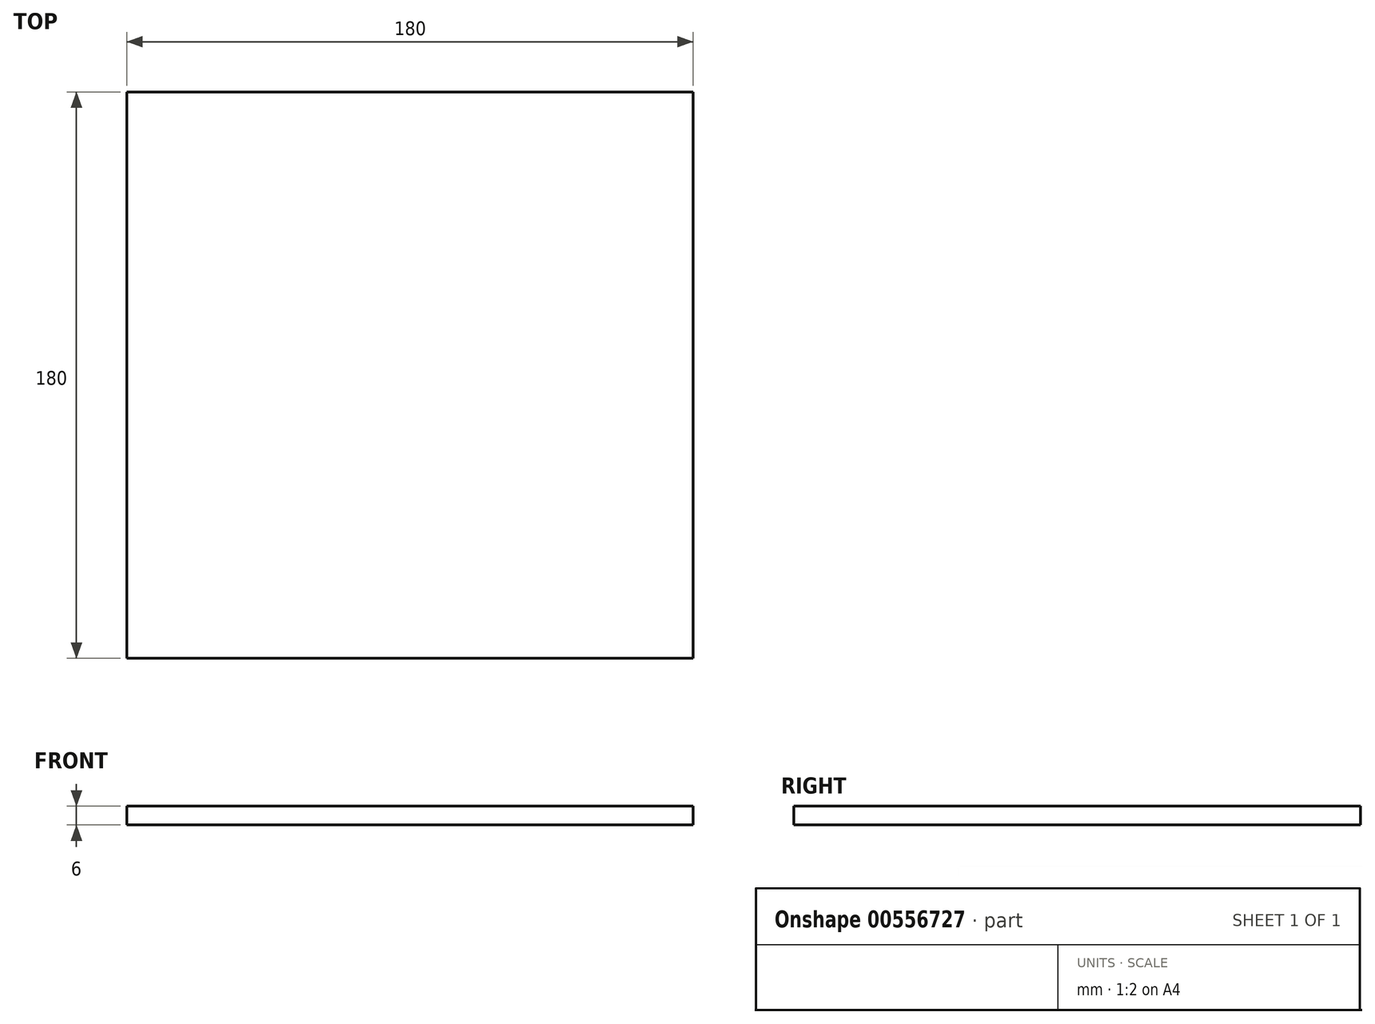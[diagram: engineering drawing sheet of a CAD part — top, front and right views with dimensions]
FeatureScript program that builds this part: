
annotation { "Feature Type Name" : "Feature", "Feature Type Description" : "" }
export const myFeature = defineFeature(function(context is Context, id is Id, definition is map)
    precondition{}
    {
        {
            var Q0;
            Q0=qCreatedBy(makeId("Top.planeOp"),FACE);
            var sketch = newSketch(context, id + "F0", { "sketchPlane" : qUnion([Q0])});
            skLineSegment(sketch, "E0", {"start": v(0, 0) * mm, "end": v(0, -180) * mm});
            skLineSegment(sketch, "E1", {"start": v(0, -180) * mm, "end": v(180, -180) * mm});
            skLineSegment(sketch, "E2", {"start": v(180, -180) * mm, "end": v(180, 0) * mm});
            skLineSegment(sketch, "E3", {"start": v(180, 0) * mm, "end": v(0, 0) * mm});
            skSolve(sketch);
        }
        {
            var Q0;
            Q0 = qSketchRegion(id + "F0", true);
            extrude(context, id + "F1", {"entities" : qUnion([Q0]), "depth" : 6 * mm, "offsetDistance" : 25 * mm});
        }
    });
